# Revit family: Bath-Freestanding-Caroma Cupid 1700a
name_source: partatom
category: Plumbing Fixtures
revit_build: Autodesk Revit 2014 (Build: 20131024_2115(x64)
units: mm (PartAtom-declared; Revit-internal decimal feet)

## types (1)
- Standard
    Assembly Code = D2010510
    CW Connection = No
    Capacity_ANZRS = 305.0 L
    Cost = 0 $
    Default Elevation = 0 mm  [stored 0 ft]
    Description = The Caroma Cupid collection offers bathroom indulgence, it’s soft edges & beauty will make a statement in any bathroom. The bath is suited to general purpose, domestic and commercial applications.
    HW Connection = No
    Height_ANZRS = 694 mm  [stored 2.2769 ft]
    Keynote = BT
    Length_ANZRS = 1700 mm  [stored 5.57743 ft]
    Manufacturer = GWA Bathrooms & Kitchens
    Material_ANZRS = PVC-Acrylic-Sanitary-White
    Model = CP7W
    ModifiedIssue_ANZRS = 20150202 $
    PlumbingMaterial_ANZRS = PVC-Acrylic-Sanitary-White
    Type Comments = Caroma Cupid Acrylic Freestanding Bath
    URL = http://specify.caroma.com.au
    Vent Connection = No
    WFU = 2
    Waste = Metal-Brass-Chrome
    Waste Connection = Yes
    Width_ANZRS = 765 mm  [stored 2.50984 ft]

note: [stored X ft] marks values corroborated as IEEE doubles in the binary element streams (Revit-internal decimal feet)

## geometry (parser evidence)
native form markers: Blend x5, Extrusion x1, Sweep x1
no freeform markers — native parametric forms only
